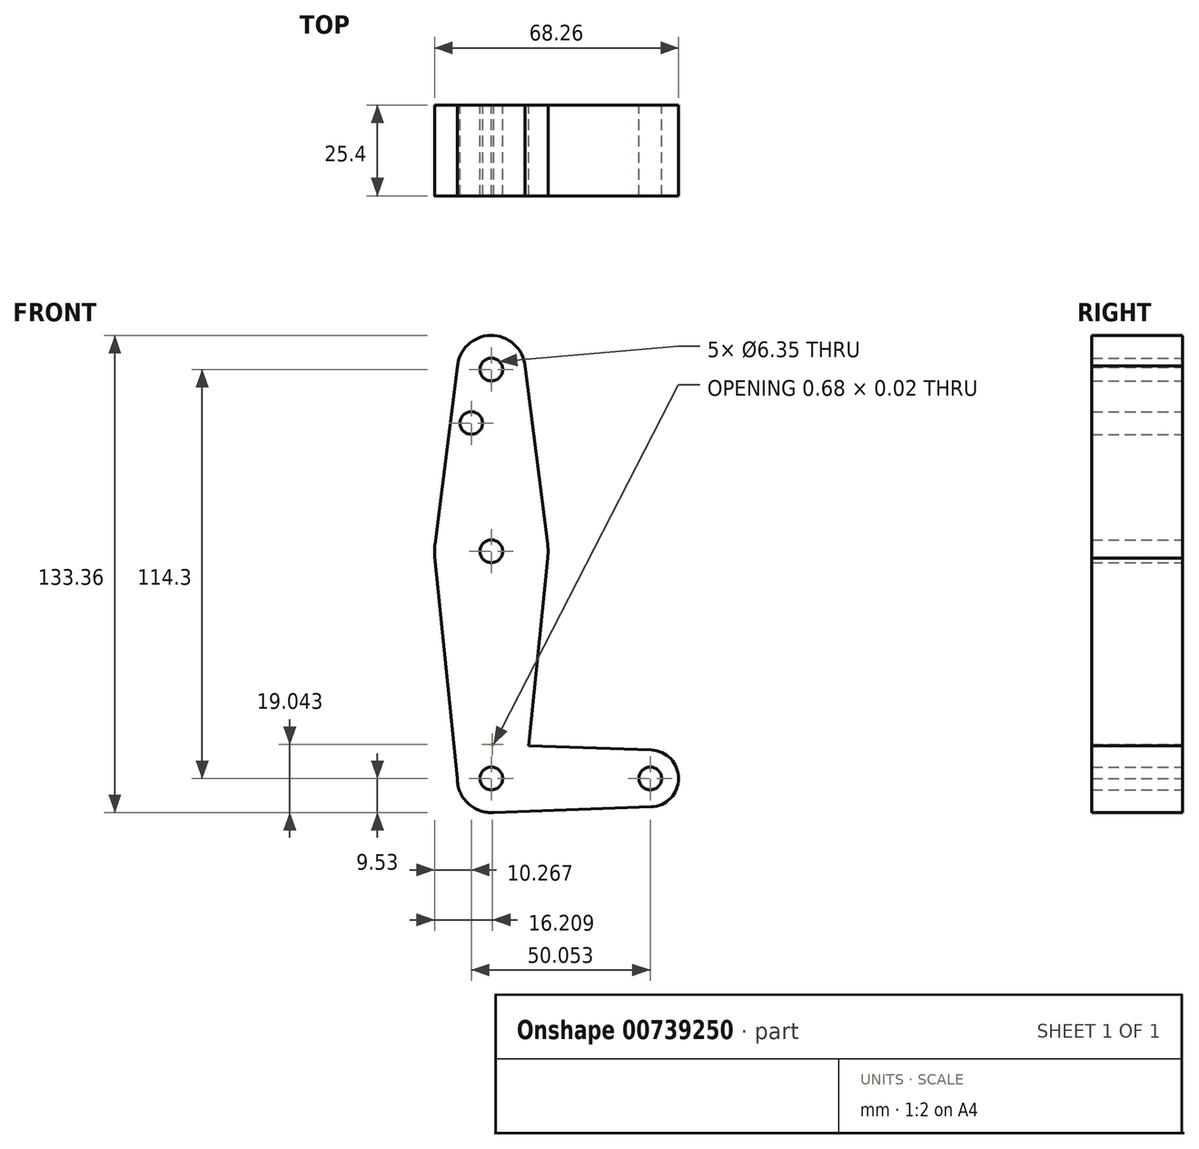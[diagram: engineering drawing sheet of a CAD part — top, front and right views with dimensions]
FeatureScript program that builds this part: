
annotation { "Feature Type Name" : "Feature", "Feature Type Description" : "" }
export const myFeature = defineFeature(function(context is Context, id is Id, definition is map)
    precondition{}
    {
        {
            var Q0;
            Q0=qCreatedBy(makeId("Front.planeOp"),FACE);
            var sketch = newSketch(context, id + "F0", { "sketchPlane" : qUnion([Q0])});
            skLineSegment(sketch, "E0", {"start": v(0, 0) * mm, "end": v(0, 114.3) * mm, "construction": true});
            skLineSegment(sketch, "E1", {"start": v(0, 0) * mm, "end": v(44.45, 0) * mm, "construction": true});
            skCircle(sketch, "E2", {"center": v(0, 0) * mm, "radius": 9.53 * mm});
            skCircle(sketch, "E3", {"center": v(0, 63.5) * mm, "radius": 15.88 * mm});
            skCircle(sketch, "E4", {"center": v(0, 114.3) * mm, "radius": 9.53 * mm});
            skCircle(sketch, "E5", {"center": v(44.45, 0) * mm, "radius": 7.94 * mm});
            skLineSegment(sketch, "E6", {"start": v(-9.5, 114.92) * mm, "end": v(-15.75, 65.49) * mm});
            skLineSegment(sketch, "E7", {"start": v(9.48, 115.26) * mm, "end": v(15.75, 65.49) * mm});
            skLineSegment(sketch, "E8", {"start": v(15.75, 61.53) * mm, "end": v(9.52, 0) * mm});
            skLineSegment(sketch, "E9", {"start": v(-9.52, 0) * mm, "end": v(-15.8, 61.9) * mm});
            skLineSegment(sketch, "E10", {"start": v(0, 9.52) * mm, "end": v(44.73, 7.93) * mm});
            skLineSegment(sketch, "E11", {"start": v(0, -9.53) * mm, "end": v(44.73, -7.93) * mm});
            skCircle(sketch, "E12", {"center": v(44.45, 0) * mm, "radius": 3.18 * mm});
            skCircle(sketch, "E13", {"center": v(-5.6, 99.34) * mm, "radius": 3.18 * mm});
            skCircle(sketch, "E14", {"center": v(0, 0) * mm, "radius": 3.18 * mm});
            skCircle(sketch, "E15", {"center": v(0, 63.5) * mm, "radius": 3.18 * mm});
            skCircle(sketch, "E16", {"center": v(0, 114.3) * mm, "radius": 3.18 * mm});
            skSolve(sketch);
        }
        {
            var Q0;
            Q0 = qSketchRegion(id + "F0", true);
            extrude(context, id + "F1", {"entities" : qUnion([Q0]), "depth" : 25.4 * mm, "offsetDistance" : 25.4 * mm});
        }
    });
